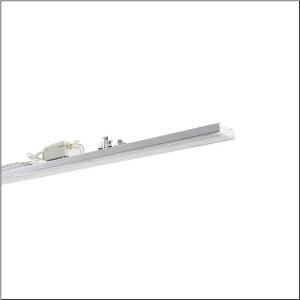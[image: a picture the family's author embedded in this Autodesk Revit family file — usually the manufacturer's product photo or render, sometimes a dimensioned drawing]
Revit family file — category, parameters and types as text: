
# Revit family: licross_21_recessed_mo_52tl12dv4fxg3s4
name_source: partatom
category: Lighting Fixtures
units: mm (PartAtom-declared; Revit-internal decimal feet)

## family parameters
Cut with Voids When Loaded = No
Host = Face
Light Source = No
Part Type = Normal
Room Calculation Point = No
Round Connector Dimension = Use Diameter
Shared = No

## types (1)
- --- (1 x LED, 950 lm, 5.5 W, 4000K)
    Apparent Load = 6 VA
    CIE Flux Codes = 72 92 99 100 100
    Color Rendering = 80
    Color Temperature = 4000K
    Default Elevation = 1800 mm
    Description = Licross 21 Recessed MO, luminaire insert, of sheet steel, galvanised, coil coated, white, length: 2.250mm, width: 66mm, height: 67mm, LED rated luminous flux: 15.420lm, light colour: 840, SDCM (Standard Deviation of Colour Matching)MacAdam ≤ 3 SDCM (initial), control gear: DALI 2, with plug, 6-pole, with phase selection, for trunking rail, 9 or 11-core, mains connection: 220..240V, AC, 50/60Hz, rated input power: 89W, for trunking rail, 9-/11-core, internal wiring halogen-free, for emergency light function, converter,control gear: single battery element, battery: LiFePO4, 9Ah, primary optical cover: cover, of PMMA, light emission: direct distribution, primary light characteristic: symmetric, protection rating (complete): IP40, insulation class (complete): insulation class I (protective earthing), certification: CE, UKCA, protection symbol: D if used in an environment without relevant dust loads with corresponding accessories, impact resistance: IK06, permissible ambient temperature for indoor applications: +5..+35°C, standard: EN 60598-2-22, LABS conformity tested according to VDMA 24364:2018-05, reducing of maximum allowable ambient temperature of 5°C with ceiling mounting, corresponds to IFS (International Featured Standards) requirements for safety and quality in the food industry, The light source and the operating device comply with the requirements of the Ecodesign Regulation (EU) 2019/2020 and are replaceable in accordance with this regulation, packaging unit: 1 piece
    Height = 58 mm
    Lamp = 1 x LED
    Lamp Light Flux = 950 lm
    Lamp Power = 5.5 W
    Lamp count = 1
    Length = 2250 mm
    Luminous efficacy = 173 lm/W
    Manufacturer = Siteco
    ModVariant = No
    Model = 52TL12DV4FXG3S4
    Mounting Place = Ceiling
    Mounting Type = Pendant
    Number of Poles = 1
    OnlyDefault = Yes
    Power Factor = 1
    Product Name = Licross 21 Recessed MO
    Product group = luminaire insert | ceiling pendant
    ProductGroupID = 901
    Protection Class = Protection class I
    Protection Degree = IP 40
    RLX_Detail_Level = 1
    RLX_Emergency_Light_Flux = 0 lm
    RLX_Emergency_Type = 0
    RLX_Emergency_Type_DB = No
    RlxData = <blob elided: 30485 chars, md5=3bac5dab>
    Socket = socket
    Standby Power = 0 W
    System Light Flux = 950 lm
    System Power = 6 W
    Type Comments = : emergency light operation: 3 h
    Type Image = l_1296930.jpg
    URL = http://relux.com
    VarID = @adj_111567
    Voltage = 0 V
    Weight = 0.00 kg
    Width = 66 mm

## geometry (parser evidence)
native form markers: Blend x4, Sweep x10
no freeform markers — native parametric forms only
